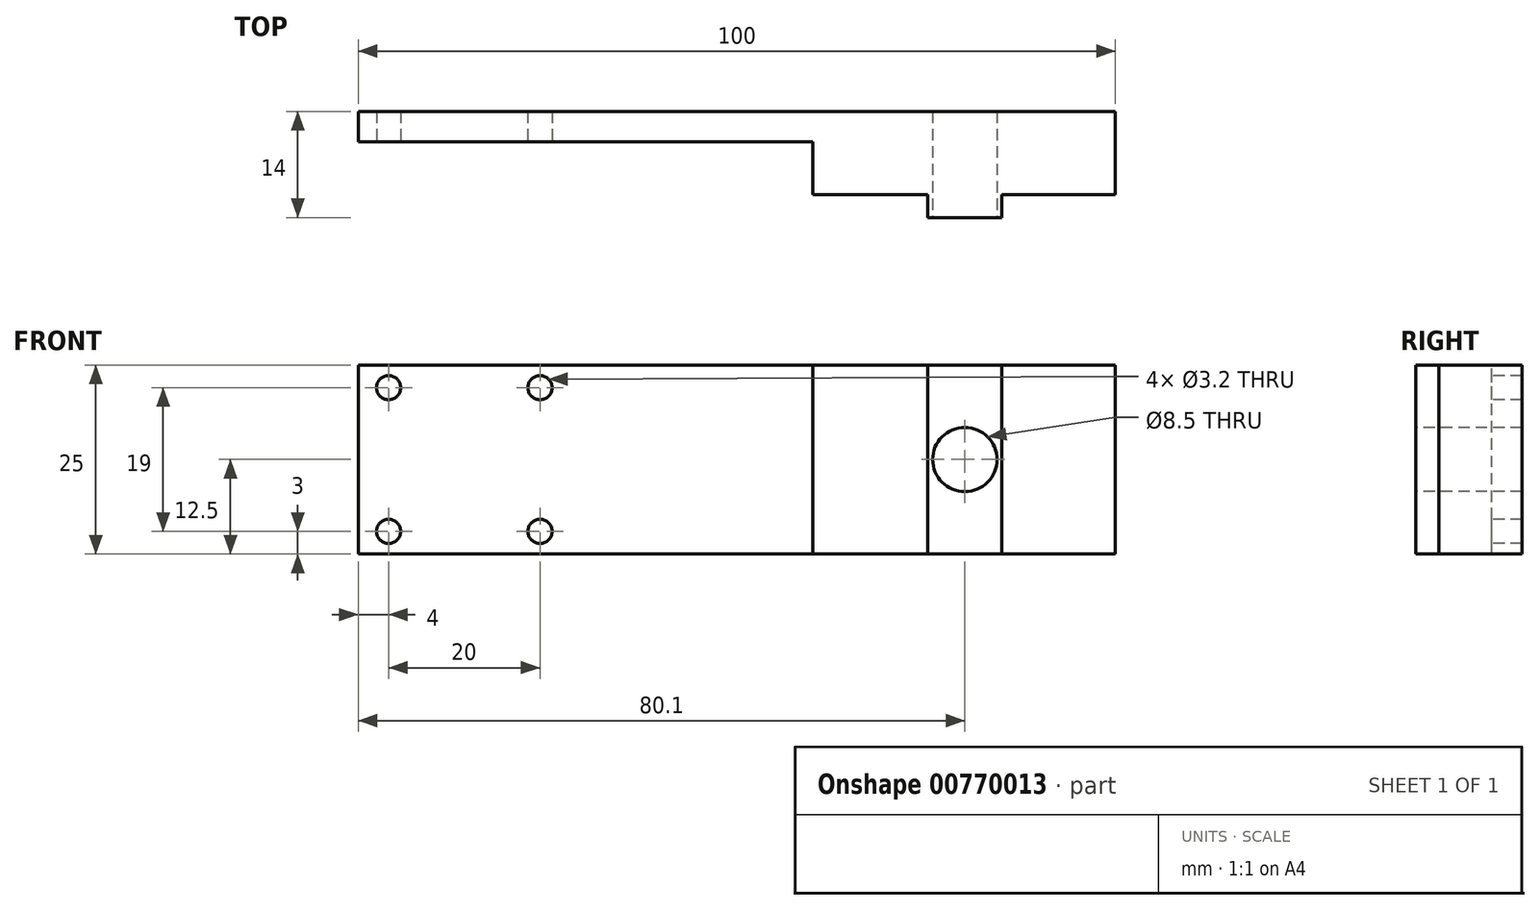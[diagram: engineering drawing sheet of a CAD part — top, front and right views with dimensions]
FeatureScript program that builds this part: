
annotation { "Feature Type Name" : "Feature", "Feature Type Description" : "" }
export const myFeature = defineFeature(function(context is Context, id is Id, definition is map)
    precondition{}
    {
        {
            var Q0;
            Q0=qCreatedBy(makeId("Front.planeOp"),FACE);
            var sketch = newSketch(context, id + "F0", { "sketchPlane" : qUnion([Q0])});
            skLineSegment(sketch, "E0.bottom", {"start": v(0, 0) * mm, "end": v(-100, 0) * mm});
            skLineSegment(sketch, "E0.top", {"start": v(0, 25) * mm, "end": v(-100, 25) * mm});
            skLineSegment(sketch, "E0.left", {"start": v(0, 0) * mm, "end": v(0, 25) * mm});
            skLineSegment(sketch, "E0.right", {"start": v(-100, 0) * mm, "end": v(-100, 25) * mm});
            skSolve(sketch);
        }
        {
            var Q0;
            Q0=qCreatedBy(makeId("Front.planeOp"),FACE);
            var sketch = newSketch(context, id + "F1", { "sketchPlane" : qUnion([Q0])});
            skSolve(sketch);
        }
        {
            var Q0;
            Q0 = qSketchRegion(id + "F1", true);
            var Q1;
            Q1=makeQuery(id+"F0.imprint","IMPRINT",FACE,{"disambiguationData":[TD([[makeQuery(id+"F0.imprint","IMPRINT",EDGE,{"derivedFrom":sQuery(id+"F0.wireOp",EDGE,"E0.bottom")}),-1.0]])]});
            extrude(context, id + "F2", {"entities" : qUnion([Q0, Q1]), "depth" : 4 * mm, "offsetDistance" : 25 * mm});
        }
        {
            var Q0;
            Q0=qCreatedBy(makeId("Front.planeOp"),FACE);
            var sketch = newSketch(context, id + "F3", { "sketchPlane" : qUnion([Q0])});
            skLineSegment(sketch, "E1.bottom", {"start": v(0, 25) * mm, "end": v(-40, 25) * mm});
            skLineSegment(sketch, "E1.top", {"start": v(0, 0) * mm, "end": v(-40, 0) * mm});
            skLineSegment(sketch, "E1.left", {"start": v(0, 25) * mm, "end": v(0, 0) * mm});
            skLineSegment(sketch, "E1.right", {"start": v(-40, 25) * mm, "end": v(-40, 0) * mm});
            skSolve(sketch);
        }
        {
            var Q0;
            Q0 = qSketchRegion(id + "F3", true);
            extrude(context, id + "F4", {"entities" : qUnion([Q0]), "operationType" : NewBodyOperationType.ADD, "depth" : 11 * mm, "offsetDistance" : 25 * mm});
        }
        {
            var Q0;
            Q0=makeQuery(id+"F4.opExtrude","CAP_FACE",FACE,{"disambiguationData":[OSD([sQuery(id+"F3.wireOp",EDGE,"E1.bottom"),sQuery(id+"F3.wireOp",EDGE,"E1.top"),sQuery(id+"F3.wireOp",EDGE,"E1.left"),sQuery(id+"F3.wireOp",EDGE,"E1.right")])],"isStart":false});
            var sketch = newSketch(context, id + "F5", { "sketchPlane" : qUnion([Q0])});
            skLineSegment(sketch, "E2.bottom", {"start": v(-15, 25) * mm, "end": v(-24.8, 25) * mm});
            skLineSegment(sketch, "E2.top", {"start": v(-15, 0) * mm, "end": v(-24.8, 0) * mm});
            skLineSegment(sketch, "E2.left", {"start": v(-15, 25) * mm, "end": v(-15, 0) * mm});
            skLineSegment(sketch, "E2.right", {"start": v(-24.8, 25) * mm, "end": v(-24.8, 0) * mm});
            skLineSegment(sketch, "E3.left", {"start": v(-15, 0) * mm, "end": v(-15, 25) * mm});
            skLineSegment(sketch, "E3.right", {"start": v(-24.8, 0) * mm, "end": v(-24.8, 25) * mm});
            skSolve(sketch);
        }
        {
            var Q0;
            Q0 = qSketchRegion(id + "F5", true);
            extrude(context, id + "F6", {"entities" : qUnion([Q0]), "operationType" : NewBodyOperationType.ADD, "depth" : 3 * mm, "offsetDistance" : 25 * mm});
        }
        {
            var Q0;
            Q0=makeQuery(id+"F2.opExtrude","CAP_FACE",FACE,{"disambiguationData":[OSD([sQuery(id+"F0.wireOp",EDGE,"E0.bottom"),sQuery(id+"F0.wireOp",EDGE,"E0.top"),sQuery(id+"F0.wireOp",EDGE,"E0.left"),sQuery(id+"F0.wireOp",EDGE,"E0.right")])],"isStart":false});
            var sketch = newSketch(context, id + "F7", { "sketchPlane" : qUnion([Q0])});
            skPoint(sketch, "E4", {"position": v(-96, 22) * mm});
            skSolve(sketch);
        }
        {
            var Q0;
            {var subQ0=sQuery(id+"F0.wireOp",EDGE,"E0.right");Q0=makeQuery(id+"F7.imprint","IMPRINT",FACE,{"disambiguationData":[TD([[makeQuery(id+"F7.imprint","IMPRINT",EDGE,{"derivedFrom":makeQuery(id+"F2.opExtrude","CAP_EDGE",EDGE,{"disambiguationData":[OSD([subQ0])],"isStart":false})}),-1.0]])]});}
            var sketch = newSketch(context, id + "F8", { "sketchPlane" : qUnion([Q0])});
            skPoint(sketch, "E5", {"position": v(-76, 22) * mm});
            skSolve(sketch);
        }
        {
            var Q0;
            Q0=sQuery(id+"F7.wireOp",VERTEX,"E4");
            var Q1;
            Q1=makeQuery(id+"F2.opExtrude","SWEPT_BODY",BODY,{"disambiguationData":[OSD([sQuery(id+"F0.wireOp",EDGE,"E0.bottom"),sQuery(id+"F0.wireOp",EDGE,"E0.top"),sQuery(id+"F0.wireOp",EDGE,"E0.left"),sQuery(id+"F0.wireOp",EDGE,"E0.right")])]});
            hole(context, id + "F9", {"style" : HoleStyle.SIMPLE, "endStyle" : HoleEndStyle.THROUGH, "holeDiameter" : 3.2 * mm, "majorDiameter" : 5 * mm, "isTappedThrough" : true, "tappedDepth" : 12 * mm, "tapClearance" : 3, "locations" : qUnion([Q0]), "scope" : qUnion([Q1])});
        }
        {
            var Q0;
            Q0=sQuery(id+"F8.wireOp",VERTEX,"E5");
            var Q1;
            Q1=makeQuery(id+"F2.opExtrude","SWEPT_BODY",BODY,{"disambiguationData":[OSD([sQuery(id+"F0.wireOp",EDGE,"E0.bottom"),sQuery(id+"F0.wireOp",EDGE,"E0.top"),sQuery(id+"F0.wireOp",EDGE,"E0.left"),sQuery(id+"F0.wireOp",EDGE,"E0.right")])]});
            hole(context, id + "F10", {"style" : HoleStyle.SIMPLE, "endStyle" : HoleEndStyle.THROUGH, "holeDiameter" : 3.2 * mm, "majorDiameter" : 5 * mm, "isTappedThrough" : true, "tappedDepth" : 12 * mm, "tapClearance" : 3, "locations" : qUnion([Q0]), "scope" : qUnion([Q1])});
        }
        {
            var Q0;
            Q0=makeQuery(id+"F6.opExtrude","CAP_FACE",FACE,{"disambiguationData":[OSD([sQuery(id+"F5.wireOp",EDGE,"E2.top"),sQuery(id+"F5.wireOp",EDGE,"E2.bottom"),sQuery(id+"F5.wireOp",EDGE,"E3.left"),sQuery(id+"F5.wireOp",EDGE,"E3.right")])],"isStart":false});
            var sketch = newSketch(context, id + "F11", { "sketchPlane" : qUnion([Q0])});
            skPoint(sketch, "E6", {"position": v(-19.9, 12.5) * mm});
            skPoint(sketch, "E6.positionSnap0", {"position": v(-24.8, 12.5) * mm});
            skSolve(sketch);
        }
        {
            var Q0;
            Q0=sQuery(id+"F11.wireOp",VERTEX,"E6");
            var Q1;
            Q1=makeQuery(id+"F2.opExtrude","SWEPT_BODY",BODY,{"disambiguationData":[OSD([sQuery(id+"F0.wireOp",EDGE,"E0.bottom"),sQuery(id+"F0.wireOp",EDGE,"E0.top"),sQuery(id+"F0.wireOp",EDGE,"E0.left"),sQuery(id+"F0.wireOp",EDGE,"E0.right")])]});
            hole(context, id + "F12", {"style" : HoleStyle.SIMPLE, "endStyle" : HoleEndStyle.THROUGH, "holeDiameter" : 8.5 * mm, "majorDiameter" : 5 * mm, "isTappedThrough" : true, "tappedDepth" : 12 * mm, "tapClearance" : 3, "locations" : qUnion([Q0]), "scope" : qUnion([Q1])});
        }
        {
            var Q0;
            Q0=makeQuery(id+"F2.opExtrude","CAP_FACE",FACE,{"disambiguationData":[OSD([sQuery(id+"F0.wireOp",EDGE,"E0.bottom"),sQuery(id+"F0.wireOp",EDGE,"E0.top"),sQuery(id+"F0.wireOp",EDGE,"E0.left"),sQuery(id+"F0.wireOp",EDGE,"E0.right")])],"isStart":false});
            var sketch = newSketch(context, id + "F13", { "sketchPlane" : qUnion([Q0])});
            skPoint(sketch, "E7", {"position": v(-96, 3) * mm});
            skPoint(sketch, "E8", {"position": v(-76, 3) * mm});
            skSolve(sketch);
        }
        {
            var Q0;
            Q0=sQuery(id+"F13.wireOp",VERTEX,"E7");
            var Q1;
            Q1=sQuery(id+"F13.wireOp",VERTEX,"E8");
            var Q2;
            Q2=makeQuery(id+"F2.opExtrude","SWEPT_BODY",BODY,{"disambiguationData":[OSD([sQuery(id+"F0.wireOp",EDGE,"E0.bottom"),sQuery(id+"F0.wireOp",EDGE,"E0.top"),sQuery(id+"F0.wireOp",EDGE,"E0.left"),sQuery(id+"F0.wireOp",EDGE,"E0.right")])]});
            hole(context, id + "F14", {"style" : HoleStyle.SIMPLE, "endStyle" : HoleEndStyle.THROUGH, "holeDiameter" : 3.2 * mm, "majorDiameter" : 5 * mm, "isTappedThrough" : true, "tappedDepth" : 12 * mm, "tapClearance" : 3, "locations" : qUnion([Q0, Q1]), "scope" : qUnion([Q2])});
        }
    });
